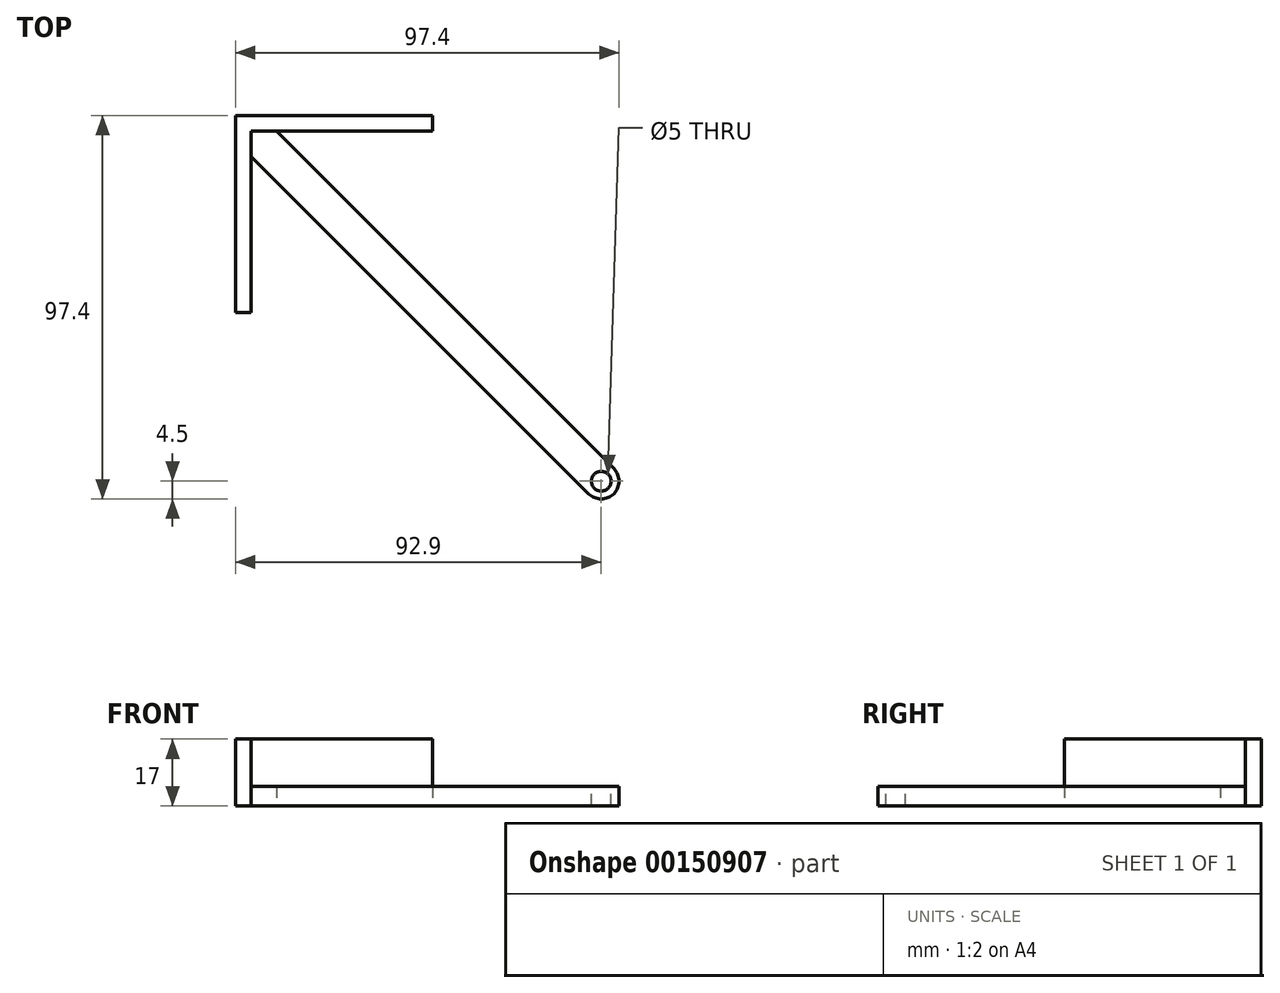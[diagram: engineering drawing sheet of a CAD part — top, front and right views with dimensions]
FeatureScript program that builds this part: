
annotation { "Feature Type Name" : "Feature", "Feature Type Description" : "" }
export const myFeature = defineFeature(function(context is Context, id is Id, definition is map)
    precondition{}
    {
        {
            var Q0;
            Q0=qCreatedBy(makeId("Top.planeOp"),FACE);
            var sketch = newSketch(context, id + "F0", { "sketchPlane" : qUnion([Q0])});
            skLineSegment(sketch, "E0", {"start": v(-92.9, 42.9) * mm, "end": v(-92.9, 92.9) * mm});
            skLineSegment(sketch, "E1", {"start": v(-92.9, 92.9) * mm, "end": v(-42.9, 92.9) * mm});
            skLineSegment(sketch, "E2", {"start": v(-42.9, 92.9) * mm, "end": v(-42.9, 88.9) * mm});
            skLineSegment(sketch, "E3", {"start": v(-42.9, 88.9) * mm, "end": v(-82.54, 88.9) * mm});
            skLineSegment(sketch, "E4", {"start": v(-82.54, 88.9) * mm, "end": v(3.18, 3.18) * mm});
            skLineSegment(sketch, "E5", {"start": v(-3.18, -3.18) * mm, "end": v(-88.9, 82.54) * mm});
            skLineSegment(sketch, "E6", {"start": v(-88.9, 82.54) * mm, "end": v(-88.9, 42.9) * mm});
            skLineSegment(sketch, "E7", {"start": v(-88.9, 42.9) * mm, "end": v(-92.9, 42.9) * mm});
            skArc(sketch, "E8", {"start": v(-3.18, -3.18) * mm, "mid": v(3.18, -3.18) * mm, "end": v(3.18, 3.18) * mm});
            skSolve(sketch);
        }
        {
            var Q0;
            Q0 = qSketchRegion(id + "F0", true);
            extrude(context, id + "F1", {"entities" : qUnion([Q0]), "depth" : 5 * mm});
        }
        {
            var Q0;
            Q0=makeQuery(id+"F1.opExtrude","CAP_FACE",FACE,{"disambiguationData":[OSD([sQuery(id+"F0.wireOp",EDGE,"E0"),sQuery(id+"F0.wireOp",EDGE,"E1"),sQuery(id+"F0.wireOp",EDGE,"E2"),sQuery(id+"F0.wireOp",EDGE,"E3"),sQuery(id+"F0.wireOp",EDGE,"E4"),sQuery(id+"F0.wireOp",EDGE,"E5"),sQuery(id+"F0.wireOp",EDGE,"E6"),sQuery(id+"F0.wireOp",EDGE,"E7"),sQuery(id+"F0.wireOp",EDGE,"E8")])],"isStart":false});
            var sketch = newSketch(context, id + "F2", { "sketchPlane" : qUnion([Q0])});
            skLineSegment(sketch, "E9.0", {"start": v(-92.9, 92.9) * mm, "end": v(-42.9, 92.9) * mm});
            skLineSegment(sketch, "E10.0", {"start": v(-92.9, 42.9) * mm, "end": v(-92.9, 92.9) * mm});
            skLineSegment(sketch, "E11", {"start": v(-92.9, 42.9) * mm, "end": v(-88.9, 42.9) * mm});
            skLineSegment(sketch, "E12", {"start": v(-88.9, 42.9) * mm, "end": v(-88.9, 88.9) * mm});
            skLineSegment(sketch, "E13", {"start": v(-88.9, 88.9) * mm, "end": v(-42.9, 88.9) * mm});
            skLineSegment(sketch, "E14", {"start": v(-42.9, 88.9) * mm, "end": v(-42.9, 92.9) * mm});
            skSolve(sketch);
        }
        {
            var Q0;
            Q0 = qSketchRegion(id + "F2", true);
            extrude(context, id + "F3", {"entities" : qUnion([Q0]), "operationType" : NewBodyOperationType.ADD, "depth" : 12 * mm});
        }
        {
            var Q0;
            Q0=makeQuery(id+"F1.opExtrude","CAP_FACE",FACE,{"disambiguationData":[OSD([sQuery(id+"F0.wireOp",EDGE,"E0"),sQuery(id+"F0.wireOp",EDGE,"E1"),sQuery(id+"F0.wireOp",EDGE,"E2"),sQuery(id+"F0.wireOp",EDGE,"E3"),sQuery(id+"F0.wireOp",EDGE,"E4"),sQuery(id+"F0.wireOp",EDGE,"E5"),sQuery(id+"F0.wireOp",EDGE,"E6"),sQuery(id+"F0.wireOp",EDGE,"E7"),sQuery(id+"F0.wireOp",EDGE,"E8")])],"isStart":false});
            var sketch = newSketch(context, id + "F4", { "sketchPlane" : qUnion([Q0])});
            skCircle(sketch, "E15", {"center": v(0, 0) * mm, "radius": 2.5 * mm});
            skSolve(sketch);
        }
        {
            var Q0;
            Q0 = qSketchRegion(id + "F4", true);
            extrude(context, id + "F5", {"entities" : qUnion([Q0]), "operationType" : NewBodyOperationType.REMOVE, "oppositeDirection" : true, "depth" : 25 * mm});
        }
    });
